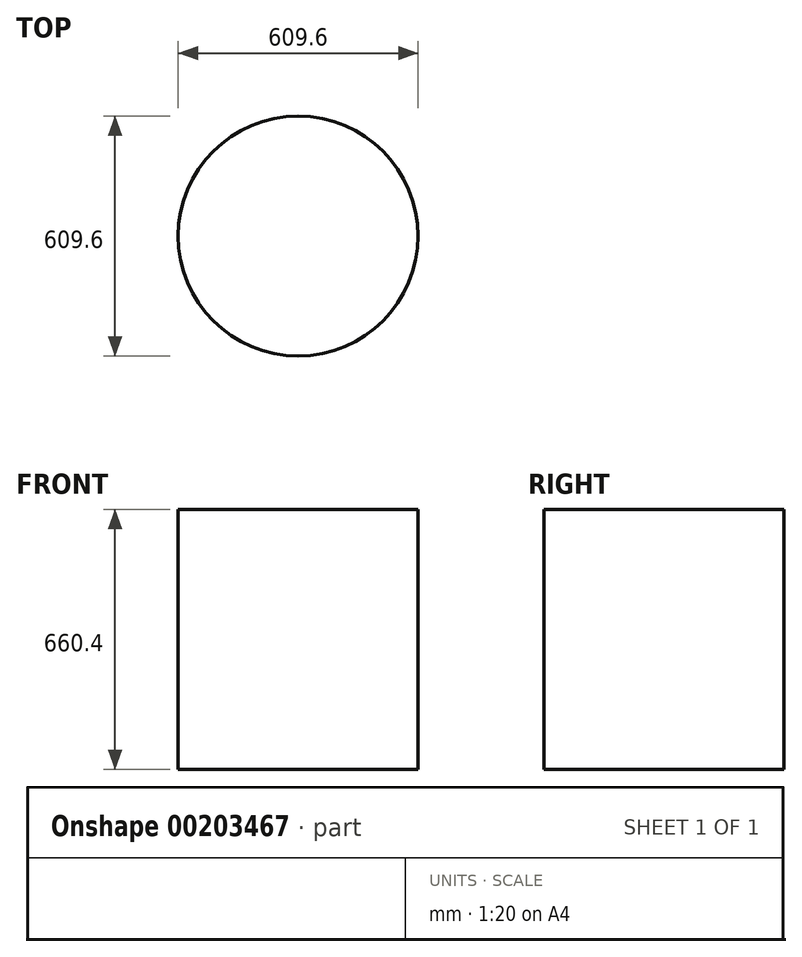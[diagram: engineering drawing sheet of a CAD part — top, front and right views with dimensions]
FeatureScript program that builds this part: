
annotation { "Feature Type Name" : "Feature", "Feature Type Description" : "" }
export const myFeature = defineFeature(function(context is Context, id is Id, definition is map)
    precondition{}
    {
        {
            var Q0;
            Q0=qCreatedBy(makeId("Top.planeOp"),FACE);
            var sketch = newSketch(context, id + "F0", { "sketchPlane" : qUnion([Q0])});
            skCircle(sketch, "E0", {"center": v(0, 0) * mm, "radius": 304.8 * mm});
            skSolve(sketch);
        }
        {
            var Q0;
            Q0 = qSketchRegion(id + "F0", true);
            extrude(context, id + "F1", {"entities" : qUnion([Q0]), "depth" : 660.4 * mm});
        }
    });
